# Revit family: QF_ELECTROLUXPROFESSIONAL_1LSNTP_WN6-28_E
name_source: partatom
category: Attrezzature speciali
units: mm (PartAtom-declared; Revit-internal decimal feet)

## family parameters
Basato su piano di lavoro = No
Condiviso = No
Punto di calcolo locali = No
Quota connettore circolare = Usa diametro
Sempre verticale = Sì
Taglio con vuoti quando caricato = No
Tipo di parte = Normale

## types (31) — shared parameters
Depth = 1030 mm  [stored 3.37927 ft]
Depth Actual = 1030 mm  [stored 3.37927 ft]
Height = 1430.8 mm  [stored 4.69423 ft]
Height Actual = 1430 mm  [stored 4.6916 ft]
Latent Heat Output = 0.0
Length Actual = 830 mm  [stored 2.7231 ft]
Modello = WN6-28
Produttore = Electrolux Professional
Sensible Heat Output = 0.0
URL = www.electroluxprofessional.com
Weight = 262
Width = 830 mm  [stored 2.7231 ft]
zero-valued in all types: Gas KW, Prospetto di default, Steam Pounds per Hour

## per-type parameters (varying)
| type | Cycle | Descrizione | Item Number | Phase | Volts | Watts |
| 9867930055 | 60 Hz | WASHER WN6-28 28KG EL 18KW 440/60/3 COMPASS PRO 6G01 ML 2xWATER POWDER VALV.OPEN SST/SILVER TRAFO DISCON. STOP | 1L8243 | 3 | 440 V | 18800 W |
| 9867930101 | 50 Hz | WASHER WN6-28 28KG EL 18KW 380-415/50/3 COMPASS PRO 6G01 ML 2xWATER POWDER VALV.OPEN SST/SILVER TRAFO DISCON. STOP | 1LSP5Y | 3 | 415 V | 18800 W |
| 9867930181 | 60 Hz | WASHER WN6-28 28KG NO HEAT 220-240/60/1N COMPASS PRO 6G01 ML 2xWATER POWDER+5xLIQ. VALV.OPEN SILVER 2.I/O QC DISCON. STO | 1LA22F | 1 | 240 V | 1100 W |
| 9867930060 | 50 Hz | WASHER WN6-28 28KG EL 18KW 380-415/50/3N COMPASS PRO 6G01 ML 2xWATER POWDER VALV.OPEN SILVER DISCON. STOP | 1L8245 | 3 | 415 V | 18800 W |
| 9867930159 | 60 Hz | WASHER WN6-28 28KG EL 18KW 480/60/3 COMPASS PRO 6G01 ML 2xWATER POWDER VALV.OPEN SILVER TRAFO DISCON. STOP | 1L0GE4 | 3 | 480 V | 18800 W |
| 9867930271 | 60 Hz | WASHER WN6-28 28KG EL 18KW 440/60/3 COMPASS PRO 6H01 ML 2xWATER POWDER+5xLIQ. VALV.OPEN SST/SILVER 2.I/O TRAFO DISCON. S | 1LM0CP | 3 | 440 V | 18800 W |
| 9867930239 | 50 Hz | WASHER WN6-28 28KG NO HEAT 220-240/50/1N COMPASS PRO 6G01 ML 2xWATER POWDER VALV.OPEN SILVER DISCON. STOP | 1LSPS5 | 1 | 240 V | 1100 W |
| 9867930269 | 50 Hz | WASHER WN6-28 28KG EL 18KW 220-240/50/3 COMPASS PRO 6G01 ML 2xWATER POWDER+5xLIQ. VALV.OPEN SILVER 2.I/O DISCON. STOP | 1LM04N | 3 | 240 V | 18800 W |
| 9867930249 | 60 Hz | WASHER WN6-28 28KG EL 18KW 220-240/60/3 COMPASS PRO 6G01 ML 2xWATER POWDER+5xLIQ. VALV.OPEN SILVER 2.I/O DISCON. STOP | 1L0HA0 | 3 | 240 V | 18800 W |
| 9867930088 | 50 Hz | WASHER WN6-28 28KG EL 18KW 380-415/50/3N COMPASS PRO 6G01 ML 2xWATER POWDER+5xLIQ. VALV.OPEN SILVER 2.I/O DISCON. STOP | 1LSP3S | 3 | 415 V | 18800 W |
| 9867930143 | 60 Hz | WASHER WN6-28 28KG EL 18KW 480/60/3 COMPASS PRO 6G07 CH-EN 2xWATER POWDER+5xLIQ. VALV.OPEN SILVER 2.I/O TRAFO DISCON. ST | 1LA1B1 | 3 | 480 V | 18800 W |
| 9867930277 | 50 Hz | WASHER WN6-28 28KG NO HEAT 220-240/50/1N COMPASS PRO 6L06 CH-EN 2xWATER POWDER+5xLIQ. VALV.OPEN SILVER 2.I/O DISCON. | 1L0HGW | 1 | 240 V | 1100 W |
| 9867930160 | 60 Hz | WASHER WN6-28 28KG EL 18KW 380-415/60/3 COMPASS PRO 6G07 SE 2xWATER POWDER VALV.OPEN SST/SILVER TRAFO DISCON. STOP | 1L0GEB | 3 | 415 V | 18800 W |
| 9867930222 | 50 Hz | WASHER WN6-28 28KG EL 18KW 380-415/50/3N COMPASS PRO 6G01 ML 2xWATER POWDER VALV.CLOSED SILVER DISCON. STOP | 1L0H03 | 3 | 415 V | 18800 W |
| 9867930212 | 60 Hz | WASHER WN6-28 28KG NO HEAT 220-240/60/3 COMPASS PRO 6L01 ML 2xWATER POWDER VALV.OPEN SILVER DISCON. | 1LSPJR | 3 | 220 V | 1100 W |
| 9867930178 | 50 Hz | WASHER WN6-28 28KG EL 18KW 380-415/50/3 COMPASS PRO 6G07 CH-EN 2xWATER POWDER VALV.OPEN SILVER TRAFO DISCON. STOP | 1LA21J | 3 | 415 V | 18800 W |
| 9867930148 | 60 Hz | WASHER WN6-28 28KG EL 18KW 440/60/3 COMPASS PRO 6G07 SE 2xWATER POWDER VALV.OPEN SILVER TRAFO DISCON. STOP | 1LSP9N | 3 | 440 V | 18800 W |
| 9867930205 | 60 Hz | WASHER WN6-28 28KG NO HEAT 115/60/1N COMPASS PRO 6G01 ML 2xWATER POWDER VALV.OPEN SILVER TRAFO DISCON. STOP | 1L0GVU | 1 | 115 V | 1100 W |
| 9867930275 | 50 Hz | WASHER WN6-28 28KG EL 18KW 440/50/3 COMPASS PRO 6G07 ML 2xWATER POWDER+5xLIQ. VALV.CLOSED SST 2.I/O TRAFO DISCON. STOP | 1L0HGD | 3 | 440 V | 18800 W |
| 9867930054 | 60 Hz | WASHER WN6-28 28KG EL 18KW 440/60/3 COMPASS PRO 6G01 ML 2xWATER POWDER+5xLIQ. VALV.OPEN SST/SILVER 2.I/O TRAFO DISCON. S | 1LSP3R | 3 | 440 V | 18800 W |
| 9867930059 | 50 Hz | WASHER WN6-28 28KG EL 18KW 380-415/50/3N COMPASS PRO 6H01 ML 2xWATER POWDER+5xLIQ. VALV.OPEN SST/SILVER 2.I/O DISCON. ST | 1L8235 | 3 | 415 V | 18800 W |
| 9867930132 | 50 Hz | WASHER WN6-28 28KG NO HEAT 220-240/50/1N COMPASS PRO 6G01 ML 2xWATER POWDER+5xLIQ. VALV.OPEN SILVER 2.I/O DISCON. STOP | 1L0GCC | 1 | 240 V | 1100 W |
| 9867930102 | 50 Hz | WASHER WN6-28 28KG NO HEAT 220-240/50/1N COMPASS PRO 6L01 ML 2xWATER POWDER VALV.OPEN SST/SILVER DISCON. | 1LSP5Z | 1 | 240 V | 1100 W |
| 9867930172 | 50 Hz | WASHER WN6-28 28KG EL 18KW 380-415/50/3 COMPASS PRO 6G07 ML 2xWATER POWDER+5xLIQ. VALV.OPEN SST/SILVER 2.I/O TRAFO DISCO | 1LSPDP | 3 | 415 V | 18800 W |
| 9867930152 | 60 Hz | WASHER WN6-28 28KG EL 18KW 480/60/3 COMPASS PRO 6G07 SE 2xWATER POWDER VALV.OPEN SST/SILVER TRAFO DISCON. STOP | 1L8263 | 3 | 480 V | 18800 W |
| 9867930192 | 60 Hz | WASHER WN6-28 28KG EL 18KW 220-240/60/3 COMPASS PRO 6L01 ML 2xWATER POWDER VALV.OPEN SILVER DISCON. | 1L0GPZ | 3 | 240 V | 18800 W |
| 9867930260 | 60 Hz | WASHER WN6-28 28KG NO HEAT 220/60/3 COMPASS PRO 6G01 CH-EN 2xWATER POWDER VALV.OPEN SILVER DISCON. STOP | 1L82CY | 3 | 220 V | 1100 W |
| 9867930134 | 50 Hz | WASHER WN6-28 28KG EL 18KW 380-415/50/3N COMPASS PRO 6G01 ML 2xWATER POWDER+5xLIQ. VALV.OPEN SST 2.I/O DISCON. STOP | 1L0GCW | 3 | 415 V | 18800 W |
| 9867930223 | 60 Hz | WASHER WN6-28 28KG EL 18KW 380-415/60/3N COMPASS PRO 6G01 ML 2xWATER POWDER+5xLIQ. VALV.OPEN SILVER 2.I/O DISCON. STOP | 1LSPNA | 3 | 415 V | 18800 W |
| 9867930236 | 50 Hz | WASHER WN6-28 28KG EL 18KW 380-415/50/3N COMPASS PRO 6H12 ML 2xWATER POWDER+5xLIQ. VALV.CLOSED SILVER SL.DRUM 2.I/O DISC | 1L82AR | 3 | 415 V | 18800 W |
| 9867930216 | 60 Hz | WASHER WN6-28 28KG EL 18KW 480/60/3 COMPASS PRO 6G07 CH-EN 2xWATER POWDER+5xLIQ. VALV.OPEN SST 2.I/O TRAFO DISCON. STOP | 1LSPLK | 3 | 440 V | 18800 W |

note: [stored X ft] marks values corroborated as IEEE doubles in the binary element streams (Revit-internal decimal feet)

## geometry (parser evidence)
native form markers: Sweep x5
no freeform markers — native parametric forms only
